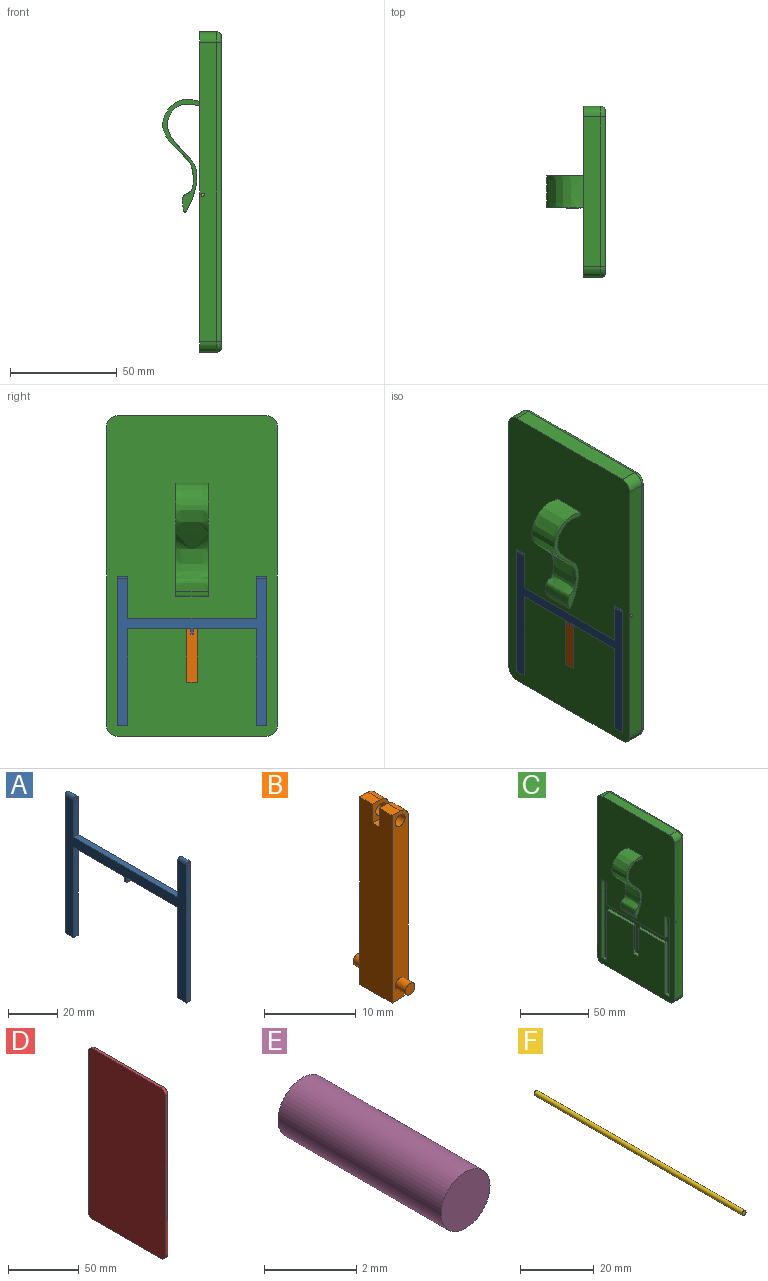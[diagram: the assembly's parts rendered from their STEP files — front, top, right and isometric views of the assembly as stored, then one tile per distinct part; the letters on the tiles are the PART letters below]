
ASSEMBLY  parts=6 mates=6
PART A: 22 faces, bbox 2.5x70x70 mm
  f0: plane 19.72x2.5mm, normal (0,1,0), area 46.9mm2, adj f6,f12,f13,f14,f21
  f1: plane 19.72x2.5mm, normal (0,-1,0), area 46.9mm2, adj f6,f12,f13,f15,f20
  f2: plane 70x2.5mm, normal (0,1,0), area 172.6mm2, adj f7,f12,f13,f15,f20
  f3: plane 70x2.5mm, normal (0,-1,0), area 172.6mm2, adj f11,f12,f13,f14,f21
  f4: cylinder r=1.25mm len=1.25mm, axis (0,-1,0), area 2mm2, adj f13,f16,f17,f19
  f5: plane 29.5x2.5mm, normal (0,0,-1), area 73.8mm2, adj f8,f12,f13,f17
  f6: plane 60x2.5mm, normal (0,0,1), area 150mm2, adj f0,f1,f12,f13
  f7: plane 5x2.5mm, normal (0,0,-1), area 12.5mm2, adj f2,f8,f12,f13
  f8: plane 45.28x2.5mm, normal (0,-1,0), area 113.2mm2, adj f5,f7,f12,f13
  f9: plane 29.5x2.5mm, normal (0,0,-1), area 73.8mm2, adj f10,f12,f13,f16
  f10: plane 45.28x2.5mm, normal (0,1,0), area 113.2mm2, adj f9,f11,f12,f13
  f11: plane 5x2.5mm, normal (0,0,-1), area 12.5mm2, adj f3,f10,f12,f13
  f12: plane 70x68.75mm, normal (-1,0,0), area 990mm2, adj f0,f1,f2,f3,f5,f6,f7,f8
  f13: plane 70x68.75mm, normal (1,0,0), area 988.8mm2, adj f0,f1,f2,f3,f4,f5,f6,f7
  f14: cylinder r=0.75mm len=5mm, axis (0,1,0), area 23.6mm2, adj f0,f3
  f15: cylinder r=0.75mm len=5mm, axis (0,1,0), area 23.6mm2, adj f1,f2
  f16: plane 2.5x2.5mm, normal (0,-1,0), area 4.1mm2, adj f4,f9,f12,f13,f18,f19
  f17: plane 2.5x2.5mm, normal (0,1,0), area 4.1mm2, adj f4,f5,f12,f13,f18,f19
  f18: cylinder r=0.75mm len=1.5mm, axis (0,-1,0), area 4.7mm2, adj f16,f17
  f19: plane 1.25x1mm, normal (0,0,-1), area 1.2mm2, adj f4,f12,f16,f17
  f20: cylinder r=1.25mm len=5mm, axis (0,-1,0), area 19.6mm2, adj f1,f2,f12,f13
  f21: cylinder r=1.25mm len=5mm, axis (0,-1,0), area 19.6mm2, adj f0,f3,f12,f13
PART B: 19 faces, bbox 2.5x8x25 mm
  f0: plane 25x2.5mm, normal (0,1,0), area 58.3mm2, adj f1,f6,f7,f9,f10,f14,f16,f18
  f1: plane 22.5x5mm, normal (1,0,0), area 111.2mm2, adj f0,f2,f3,f5,f8,f16,f17,f18
  f2: plane 2.5x2.5mm, normal (0,1,0), area 4.1mm2, adj f1,f4,f5,f9,f11,f17
  f3: plane 2.5x2.5mm, normal (0,-1,0), area 4.1mm2, adj f1,f5,f6,f9,f10,f16
  f4: plane 2x1.25mm, normal (0,0,1), area 2.5mm2, adj f2,f8,f9,f17
  f5: plane 2.5x1mm, normal (0,0,1), area 2.5mm2, adj f1,f2,f3,f9
  f6: plane 2x1.25mm, normal (0,0,1), area 2.5mm2, adj f0,f3,f9,f16
  f7: plane 5x1.25mm, normal (0,0,-1), area 6.2mm2, adj f0,f8,f9,f18
  f8: plane 25x2.5mm, normal (0,-1,0), area 58.3mm2, adj f1,f4,f7,f9,f11,f12,f17,f18
  f9: plane 25x5mm, normal (-1,0,0), area 122.5mm2, adj f0,f2,f3,f4,f5,f6,f7,f8
  f10: cylinder r=0.75mm len=2mm, axis (0,-1,0), area 9.4mm2, adj f0,f3
  f11: cylinder r=0.75mm len=2mm, axis (0,-1,0), area 9.4mm2, adj f2,f8
  f12: cylinder r=0.75mm len=1.5mm, axis (0,1,0), area 7.1mm2, adj f8,f13
  f13: plane 1.5x1.5mm, normal (0,-1,0), area 1.8mm2, adj f12
  f14: cylinder r=0.75mm len=1.5mm, axis (0,-1,0), area 7.1mm2, adj f0,f15
  f15: plane 1.5x1.5mm, normal (0,1,0), area 1.8mm2, adj f14
  f16: cylinder r=1.25mm len=2mm, axis (0,-1,0), area 3.9mm2, adj f0,f1,f3,f6
  f17: cylinder r=1.25mm len=2mm, axis (0,-1,0), area 3.9mm2, adj f1,f2,f4,f8
  f18: cylinder r=1.25mm len=5mm, axis (0,-1,0), area 9.8mm2, adj f0,f1,f7,f8
PART C: 64 faces, bbox 28.3x80.8x150.8 mm
  f0: plane 25x2.5mm, normal (0,1,0), area 28.8mm2, adj f3,f45,f49,f53,f58,f59,f60,f63
  f1: plane 25x2.5mm, normal (0,-1,0), area 28.8mm2, adj f2,f3,f49,f53,f54,f55,f56,f62
  f2: plane 27.5x2.5mm, normal (0,0,1), area 68.8mm2, adj f1,f3,f44,f49
  f3: plane 150x80mm, normal (-1,0,0), area 10823.2mm2, adj f0,f1,f2,f8,f9,f10,f11,f12
  f4: plane 1.42x1.42mm, normal (1,0,0), area 0.1mm2, adj f23,f31
  f5: plane 1.42x1.42mm, normal (1,0,0), area 0.1mm2, adj f21,f30
  f6: plane 1.42x1.42mm, normal (1,0,0), area 0.1mm2, adj f17,f27
  f7: plane 1.42x1.42mm, normal (1,0,0), area 0.1mm2, adj f19,f26
  f8: cylinder r=5mm len=8mm, axis (-1,0,0), area 62.8mm2, adj f3,f9,f15,f26
  f9: plane 70x8mm, normal (0,0,-1), area 560mm2, adj f3,f8,f10,f28
  f10: cylinder r=5mm len=8mm, axis (-1,0,0), area 62.8mm2, adj f3,f9,f11,f30
  f11: plane 140x8mm, normal (0,1,0), area 1118.2mm2, adj f3,f10,f12,f32,f51
  f12: cylinder r=5mm len=8mm, axis (-1,0,0), area 62.8mm2, adj f3,f11,f13,f31
  f13: plane 70x8mm, normal (0,0,1), area 560mm2, adj f3,f12,f14,f29
  f14: cylinder r=5mm len=8mm, axis (-1,0,0), area 62.8mm2, adj f3,f13,f15,f27
  f15: plane 140x8mm, normal (0,-1,0), area 1118.2mm2, adj f3,f8,f14,f25,f50
  f16: plane 67.07x2.43mm, normal (0,0,-1), area 162.8mm2, adj f17,f23,f24,f29
  f17: cylinder r=5mm len=5mm, axis (1,0,0), area 19.5mm2, adj f6,f16,f18,f24,f25,f27,f29
  f18: plane 137.07x2.43mm, normal (0,1,0), area 332.7mm2, adj f17,f19,f24,f25
  f19: cylinder r=5mm len=5mm, axis (1,0,0), area 19.5mm2, adj f7,f18,f20,f24,f25,f26,f28
  f20: plane 67.07x2.43mm, normal (0,0,1), area 162.8mm2, adj f19,f21,f24,f28
  f21: cylinder r=5mm len=5mm, axis (1,0,0), area 19.5mm2, adj f5,f20,f22,f24,f28,f30,f32
  f22: plane 137.07x2.43mm, normal (0,-1,0), area 332.7mm2, adj f21,f23,f24,f32
  f23: cylinder r=5mm len=5mm, axis (1,0,0), area 19.5mm2, adj f4,f16,f22,f24,f29,f31,f32
  f24: plane 147.07x77.07mm, normal (1,0,0), area 11313.5mm2, adj f16,f17,f18,f19,f20,f21,f22,f23
  f25: cylinder r=2mm len=140mm, axis (0,0,-1), area 364.3mm2, adj f15,f17,f18,f19,f26,f27
  f26: torus R=3mm, axis (1,0,0), area 20.6mm2, adj f7,f8,f19,f25,f28
  f27: torus R=3mm, axis (1,0,0), area 20.6mm2, adj f6,f14,f17,f25,f29
  f28: cylinder r=2mm len=70mm, axis (0,1,0), area 182.3mm2, adj f9,f19,f20,f21,f26,f30
  f29: cylinder r=2mm len=70mm, axis (0,1,0), area 182.3mm2, adj f13,f16,f17,f23,f27,f31
  f30: torus R=3mm, axis (1,0,0), area 20.6mm2, adj f5,f10,f21,f28,f32
  f31: torus R=3mm, axis (1,0,0), area 20.6mm2, adj f4,f12,f23,f29,f32
  f32: cylinder r=2mm len=140mm, axis (0,0,-1), area 364.3mm2, adj f11,f21,f22,f23,f30,f31
  f33: extruded ~50.75x17.39mm, area 1054.3mm2, adj f3,f34,f35,f36
  f34: extruded ~50.58x15.24mm, area 1052.6mm2, adj f3,f33,f35,f36
  f35: plane 54.17x18.34mm, normal (0,-1,0), area 138.1mm2, adj f3,f33,f34
  f36: plane 54.17x18.34mm, normal (0,1,0), area 138.1mm2, adj f3,f33,f34
  f37: plane 5x2.5mm, normal (0,0,-1), area 12.5mm2, adj f3,f38,f48,f49
  f38: plane 19.72x2.5mm, normal (0,-1,0), area 47.5mm2, adj f3,f37,f39,f49,f52
  f39: plane 60x2.5mm, normal (0,0,-1), area 150mm2, adj f3,f38,f40,f49
  f40: plane 19.72x2.5mm, normal (0,1,0), area 47.5mm2, adj f3,f39,f41,f49,f52
  f41: plane 5x2.5mm, normal (0,0,-1), area 12.5mm2, adj f3,f40,f42,f49
  f42: plane 70x2.5mm, normal (0,-1,0), area 173.2mm2, adj f3,f41,f43,f49,f51
  f43: plane 5x2.5mm, normal (0,0,1), area 12.5mm2, adj f3,f42,f44,f49
  f44: plane 45.28x2.5mm, normal (0,1,0), area 113.2mm2, adj f2,f3,f43,f49
  f45: plane 27.5x2.5mm, normal (0,0,1), area 68.8mm2, adj f0,f3,f46,f49
  f46: plane 45.28x2.5mm, normal (0,-1,0), area 113.2mm2, adj f3,f45,f47,f49
  f47: plane 5x2.5mm, normal (0,0,1), area 12.5mm2, adj f3,f46,f48,f49
  f48: plane 70x2.5mm, normal (0,1,0), area 173.2mm2, adj f3,f37,f47,f49,f50
  f49: plane 70x70mm, normal (-1,0,0), area 1125mm2, adj f0,f1,f2,f37,f38,f39,f40,f41
  f50: cylinder r=0.75mm len=5mm, axis (0,1,0), area 23.6mm2, adj f15,f48
  f51: cylinder r=0.75mm len=5mm, axis (0,1,0), area 23.6mm2, adj f11,f42
  f52: cylinder r=0.75mm len=60mm, axis (0,1,0), area 282.7mm2, adj f38,f40
  f53: plane 5x2.5mm, normal (0,0,1), area 12.5mm2, adj f0,f1,f3,f49
  f54: plane 22.5x1.5mm, normal (-1,0,0), area 33.7mm2, adj f1,f55,f56,f57
  f55: plane 1.5x1.5mm, normal (0,0,1), area 2.2mm2, adj f1,f54,f57,f62
  f56: plane 1.5x1.5mm, normal (0,0,-1), area 2.2mm2, adj f1,f54,f57,f62
  f57: plane 22.5x1.5mm, normal (0,-1,0), area 33.7mm2, adj f54,f55,f56,f62
  f58: plane 1.5x1.5mm, normal (0,0,-1), area 2.2mm2, adj f0,f60,f61,f63
  f59: plane 1.5x1.5mm, normal (0,0,1), area 2.2mm2, adj f0,f60,f61,f63
  f60: plane 22.5x1.5mm, normal (-1,0,0), area 33.8mm2, adj f0,f58,f59,f61
  f61: plane 22.5x1.5mm, normal (0,1,0), area 33.7mm2, adj f58,f59,f60,f63
  f62: plane 22.5x1.5mm, normal (1,0,0), area 33.8mm2, adj f1,f55,f56,f57
  f63: plane 22.5x1.5mm, normal (1,0,0), area 33.7mm2, adj f0,f58,f59,f61
PART D: 10 faces, bbox 2.5x77.1x147.1 mm
  f0: plane 67.07x2.5mm, normal (0,0,1), area 167.7mm2, adj f1,f7,f8,f9
  f1: cylinder r=5mm len=5mm, axis (-1,0,0), area 19.6mm2, adj f0,f2,f8,f9
  f2: plane 137.07x2.5mm, normal (0,-1,0), area 342.7mm2, adj f1,f3,f8,f9
  f3: cylinder r=5mm len=5mm, axis (-1,0,0), area 19.6mm2, adj f2,f4,f8,f9
  f4: plane 67.07x2.5mm, normal (0,0,-1), area 167.7mm2, adj f3,f5,f8,f9
  f5: cylinder r=5mm len=5mm, axis (-1,0,0), area 19.6mm2, adj f4,f6,f8,f9
  f6: plane 137.07x2.5mm, normal (0,1,0), area 342.7mm2, adj f5,f7,f8,f9
  f7: cylinder r=5mm len=5mm, axis (-1,0,0), area 19.6mm2, adj f0,f6,f8,f9
  f8: plane 147.07x77.07mm, normal (1,0,0), area 11313.5mm2, adj f0,f1,f2,f3,f4,f5,f6,f7
  f9: plane 147.07x77.07mm, normal (-1,0,0), area 11313.5mm2, adj f0,f1,f2,f3,f4,f5,f6,f7
PART E: 3 faces, bbox 1.5x5x1.5 mm
  f0: plane 1.5x1.5mm, normal (0,1,0), area 1.8mm2, adj f2
  f1: plane 1.5x1.5mm, normal (0,-1,0), area 1.8mm2, adj f2
  f2: cylinder r=0.75mm len=5mm, axis (0,-1,0), area 23.6mm2, adj f0,f1
PART F: 3 faces, bbox 1.5x80x1.5 mm
  f0: plane 1.5x1.5mm, normal (0,-1,0), area 1.8mm2, adj f1
  f1: cylinder r=0.75mm len=80mm, axis (0,1,0), area 377mm2, adj f0,f2
  f2: plane 1.5x1.5mm, normal (0,1,0), area 1.8mm2, adj f1
PLACE A t=(-54.15,-12.15,36.17)mm
PLACE B t=(-54.15,-12.15,36.17)mm
PLACE C t=(-54.15,-12.15,36.17)mm fixed
PLACE D rot(axis=(0,1,0),180deg) t=(-46.65,-12.15,36.17)mm
PLACE E t=(-54.15,-12.15,36.17)mm
PLACE F t=(-54.15,-12.15,36.17)mm
MATE planar B.f14 <-> C.f57  axis (0,1,0) through (-57.9,-8.15,-11.55)mm
MATE fastened F.f1 <-> C.f50  axis (0,-1,0) through (-57.9,-52.15,34.92)mm
MATE revolute B.f10 <-> E.f2  axis (0,1,0) through (-57.9,-12.15,10.2)mm
MATE revolute A.f20 <-> C.f50  axis (0,-1,0) through (-57.9,-47.15,34.92)mm
MATE fastened E.f2 <-> A.f4  axis (0,-1,0) through (-57.9,-12.15,10.2)mm
MATE fastened D.f8 <-> C.f24  axis (-1,0,0) through (-51.65,-12.15,36.17)mm
